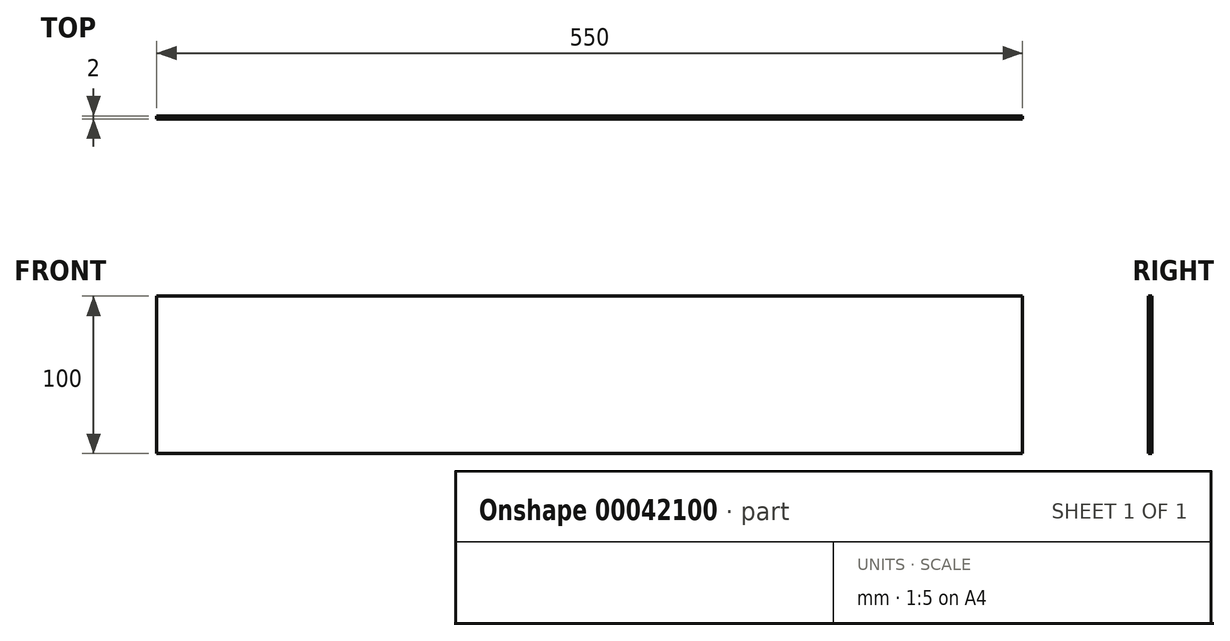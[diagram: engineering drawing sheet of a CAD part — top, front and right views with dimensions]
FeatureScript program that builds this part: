
annotation { "Feature Type Name" : "Feature", "Feature Type Description" : "" }
export const myFeature = defineFeature(function(context is Context, id is Id, definition is map)
    precondition{}
    {
        {
            var Q0;
            Q0=qCreatedBy(makeId("Front.planeOp"),FACE);
            var sketch = newSketch(context, id + "F0", { "sketchPlane" : qUnion([Q0])});
            skLineSegment(sketch, "E0.rect.bottom", {"start": v(275, -50) * mm, "end": v(-275, -50) * mm});
            skLineSegment(sketch, "E0.rect.top", {"start": v(275, 50) * mm, "end": v(-275, 50) * mm});
            skLineSegment(sketch, "E0.rect.left", {"start": v(275, -50) * mm, "end": v(275, 50) * mm});
            skLineSegment(sketch, "E0.rect.right", {"start": v(-275, -50) * mm, "end": v(-275, 50) * mm});
            skPoint(sketch, "E0.rect.middle", {"position": v(0, 0) * mm});
            skSolve(sketch);
        }
        {
            var Q0;
            Q0 = qSketchRegion(id + "F0", true);
            extrude(context, id + "F1", {"entities" : qUnion([Q0]), "depth" : 2 * mm});
        }
    });
